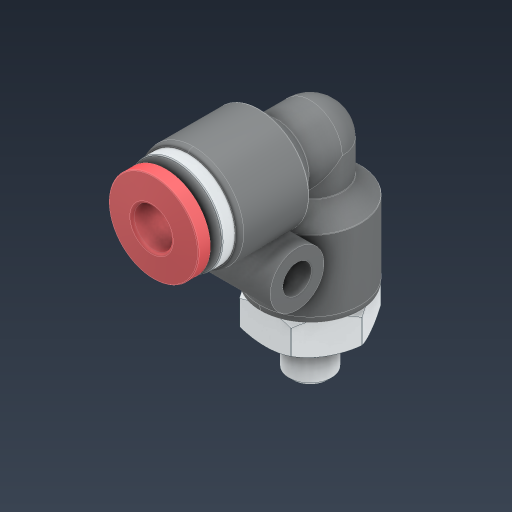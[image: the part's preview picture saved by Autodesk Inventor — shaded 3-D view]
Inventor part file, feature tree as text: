
AUTODESK INVENTOR PART (.ipt)
format: ipt  version: 2024.3 (Build 283343000, 343)  size: 480,256 bytes
history: native  units: in
note: dims shown in document units (in); Inventor stores cm internally (conversion verified against a paired STEP export)
features: other x5, revolve x1
ambient origin geometry x8: Origin, YZ Plane, XZ Plane, XY Plane, X Axis, Y Axis, Z Axis, Center Point
bodies: Solid1 (feature_tree), Solid2 (feature_tree), Solid3 (feature_tree), Solid4 (feature_tree), Solid5 (feature_tree)
feature tree (6):
  other  "Elbow Fitting1"
  revolve  "Revolve3"  [1 undecoded]
  other  "Cut-Extrude1"
  other  "_276-8637-002 Rev1_-_Fillet2_"
  other  "_276-8637-002 Rev1_-_Fillet4_"
  parser-record x1  (decoder bookkeeping rows leaked as tree rows — omitted from the tree; the rows remain in map.json)
note: 1 required parameter value undecoded (feature->parameter linkage not recoverable at this tier; creation-order binding heuristic only, values carry confidence <= 0.55)
